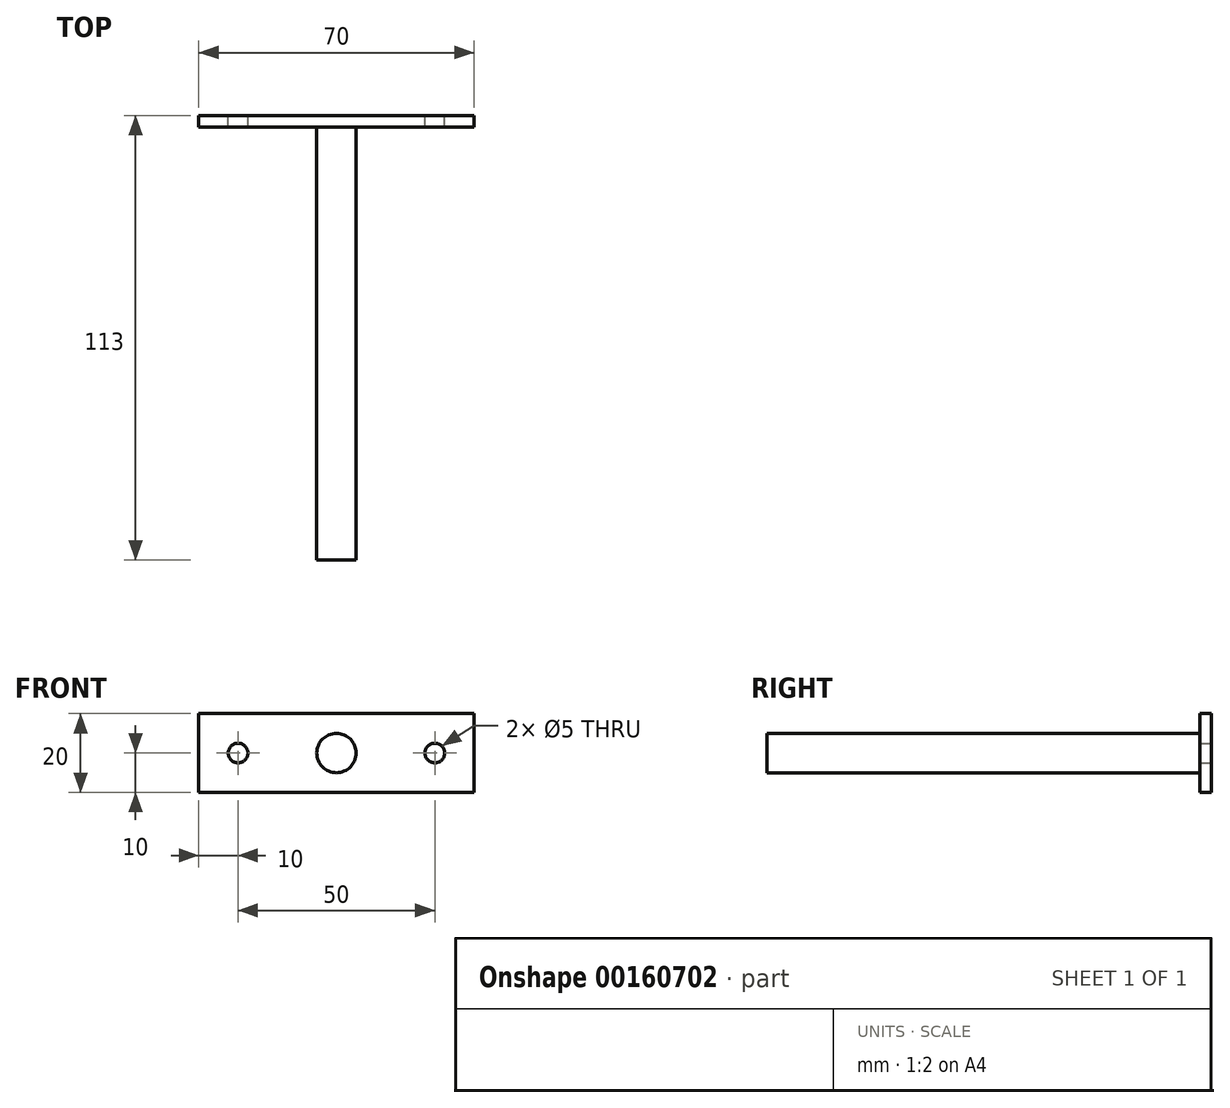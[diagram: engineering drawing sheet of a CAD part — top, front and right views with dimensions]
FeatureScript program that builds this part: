
annotation { "Feature Type Name" : "Feature", "Feature Type Description" : "" }
export const myFeature = defineFeature(function(context is Context, id is Id, definition is map)
    precondition{}
    {
        {
            var Q0;
            Q0=qCreatedBy(makeId("Front.planeOp"),FACE);
            var sketch = newSketch(context, id + "F0", { "sketchPlane" : qUnion([Q0])});
            skLineSegment(sketch, "E0.bottom", {"start": v(-35, 10) * mm, "end": v(35, 10) * mm});
            skLineSegment(sketch, "E0.top", {"start": v(-35, -10) * mm, "end": v(35, -10) * mm});
            skLineSegment(sketch, "E0.left", {"start": v(-35, 10) * mm, "end": v(-35, -10) * mm});
            skLineSegment(sketch, "E0.right", {"start": v(35, 10) * mm, "end": v(35, -10) * mm});
            skCircle(sketch, "E1", {"center": v(-25, 0) * mm, "radius": 2.5 * mm});
            skCircle(sketch, "E2.MirrorC", {"center": v(25, 0) * mm, "radius": 2.5 * mm});
            skSolve(sketch);
        }
        {
            var Q0;
            Q0=makeQuery(id+"F0.imprint","IMPRINT",FACE,{"disambiguationData":[TD([[makeQuery(id+"F0.imprint","IMPRINT",EDGE,{"derivedFrom":sQuery(id+"F0.wireOp",EDGE,"E0.bottom")}),-1.0]])]});
            extrude(context, id + "F1", {"entities" : qUnion([Q0]), "depth" : 3 * mm});
        }
        {
            var Q0;
            Q0=makeQuery(id+"F1.opExtrude","CAP_FACE",FACE,{"disambiguationData":[OSD([sQuery(id+"F0.wireOp",EDGE,"E0.bottom"),sQuery(id+"F0.wireOp",EDGE,"E0.top"),sQuery(id+"F0.wireOp",EDGE,"E0.left"),sQuery(id+"F0.wireOp",EDGE,"E0.right"),sQuery(id+"F0.wireOp",EDGE,"E1"),sQuery(id+"F0.wireOp",EDGE,"E2.MirrorC")])],"isStart":false});
            var sketch = newSketch(context, id + "F2", { "sketchPlane" : qUnion([Q0])});
            skCircle(sketch, "E3", {"center": v(0, 0) * mm, "radius": 5 * mm});
            skSolve(sketch);
        }
        {
            var Q0;
            Q0=makeQuery(id+"F2.imprint","IMPRINT",FACE,{"disambiguationData":[TD([[makeQuery(id+"F2.imprint","IMPRINT",EDGE,{"derivedFrom":sQuery(id+"F2.wireOp",EDGE,"E3")}),1.0]])]});
            var Q1;
            Q1=sQuery(id+"F2.wireOp",EDGE,"E3");
            extrude(context, id + "F3", {"entities" : qUnion([Q0]), "operationType" : NewBodyOperationType.ADD, "surfaceEntities" : qUnion([Q1]), "depth" : 110 * mm});
        }
    });
